# Revit family: Cabinet_Wall_Doors
name_source: partatom
category: Casework
units: mm (PartAtom-declared; Revit-internal decimal feet)

## family parameters
Always vertical = Yes
Classification Number = 23.40.35.11.11
Cut with Voids When Loaded = No
Room Calculation Point = No
Shared = No
Work Plane-Based = No

## types (160) — shared parameters
Assembly Code = C1030410
Building Codes = http://www.iccsafe.org
Construction Details = http://www.arcat.com
Default Elevation = 0' - 0"
Depth = 1' - 0"
Door Finish = <By Category>
Door Frame Material = ARCAT - Wood - Cherry_Domestic
Door Panel Material = ARCAT - Wood - Cherry_Domestic
Door Thickness = 0' - 0 3/4"
Expected Lifespan (Years) = 20
Frame Finish = ARCAT - Wood - Maple_Hard
Frame Width = 0' - 1 1/2"
FrameReveal = 0' - 0 1/4"
Glass Type = ARCAT - Glass - Annealed - Tinted_Green
Green Building-LEED = http://www.arcat.com
Hardware Type = Recessed Cup Self Closing Hinges
Installation Phase = Finish Carpentry
Installation_Fabricaton = http://www.nkba.org
Keynote = 12350
Left Side Panel Finish = ARCAT - Wood - Maple_Hard
Maintainence Schedule (Months) = 1
Manufacturer = Generic
Manufacturer Fax = (203) 939-2444
Manufacturer Website = http://www.arcat.com
Mounting Height = 4' - 6"
Panel Thickness = 0' - 0 3/4"
Product Data = http://www.arcat.com
Product Properties = http://www.arcat.com
Right Side Panel Finish = ARCAT - Wood - Maple_Hard
Specification = http://www.arcat.com
Warranty Duration (Years) = 5

## per-type parameters (varying)
| type | Description | Door Style | DoorCount | Height | Model | Width |
| 42x42h - 2Dr_Glz | 42"W x 42"H 2 Glass Door Wall Cabinet | Door - Shaker-Glass : Door | 2 | 3' - 6" | 42x42h - 2Dr - Glz | 3' - 6" |
| 36x42h - 2Dr_Glz | 36"W x 42"H 2 Glass Door Wall Cabinet | Door - Shaker-Glass : Door | 2 | 3' - 6" | 36x42h - 2Dr - Glz | 3' - 0" |
| 30x42h - 2Dr_Glz | 30"W x 42"H 2 Glass Door Wall Cabinet | Door - Shaker-Glass : Door | 2 | 3' - 6" | 30x42h - 2Dr - Glz | 2' - 6" |
| 24x42h - 2Dr_Glz | 24"W x 42"H 2 Glass Door Wall Cabinet | Door - Shaker-Glass : Door | 2 | 3' - 6" | 24x42h - 2Dr - Glz | 2' - 0" |
| 21x42h - 2Dr_Glz | 21"W x 42"H 2 Glass Door Wall Cabinet | Door - Shaker-Glass : Door | 2 | 3' - 6" | 21x42h - 2Dr - Glz | 1' - 9" |
| 21x42h - 1Dr_Glz | 21"W x 42"H 1 Glass Door Wall Cabinet | Door - Shaker-Glass : Door | 1 | 3' - 6" | 21x42h - 1Dr - Glz | 1' - 9" |
| 18x42h - 2Dr_Glz | 18"W x 42"H 2 Glass Door Wall Cabinet | Door - Shaker-Glass : Door | 2 | 3' - 6" | 18x42h - 2Dr - Glz | 1' - 6" |
| 18x42h - 1Dr_Glz | 18"W x 42"H 1 Glass Door Wall Cabinet | Door - Shaker-Glass : Door | 1 | 3' - 6" | 18x42h - 1Dr - Glz | 1' - 6" |
| 15x42h - 1Dr_Glz | 15"W x 42"H 1 Glass Door Wall Cabinet | Door - Shaker-Glass : Door | 1 | 3' - 6" | 15x42h - 1Dr - Glz | 1' - 3" |
| 12x42h - 1Dr_Glz | 12"W x 42"H 1 Glass Door Wall Cabinet | Door - Shaker-Glass : Door | 1 | 3' - 6" | 12x42h - 1Dr - Glz | 1' - 0" |
| 42x42h - 2Dr | 42"W x 42"H 2 Door Wall Cabinet | Door - Shaker : Door | 2 | 3' - 6" | 42x42h - 2Dr | 3' - 6" |
| 36x42h - 2Dr | 36"W x 42"H 2 Door Wall Cabinet | Door - Shaker : Door | 2 | 3' - 6" | 36x42h - 2Dr | 3' - 0" |
| 30x42h - 2Dr | 30"W x 42"H 2 Door Wall Cabinet | Door - Shaker : Door | 2 | 3' - 6" | 30x42h - 2Dr | 2' - 6" |
| 24x42h - 2Dr | 24"W x 42"H 2 Door Wall Cabinet | Door - Shaker : Door | 2 | 3' - 6" | 24x42h - 2Dr | 2' - 0" |
| 21x42h - 2Dr | 21"W x 42"H 2 Door Wall Cabinet | Door - Shaker : Door | 2 | 3' - 6" | 21x42h - 2Dr | 1' - 9" |
| 21x42h - 1Dr | 21"W x 42"H 1 Door Wall Cabinet | Door - Shaker : Door | 1 | 3' - 6" | 21x42h - 1Dr | 1' - 9" |
| 18x42h - 2Dr | 18"W x 42"H 2 Door Wall Cabinet | Door - Shaker : Door | 2 | 3' - 6" | 18x42h - 2Dr | 1' - 6" |
| 18x42h - 1Dr | 18"W x 42"H 1 Door Wall Cabinet | Door - Shaker : Door | 1 | 3' - 6" | 18x42h - 1Dr | 1' - 6" |
| 15x42h - 1Dr | 15"W x 42"H 1 Door Wall Cabinet | Door - Shaker : Door | 1 | 3' - 6" | 15x42h - 1Dr | 1' - 3" |
| 12x42h - 1Dr | 12"W x 42"H 1 Door Wall Cabinet | Door - Shaker : Door | 1 | 3' - 6" | 12x42h - 1Dr | 1' - 0" |
| 42x36h - 2Dr_Glz | 42"W x 36"H 2 Glass Door Wall Cabinet | Door - Shaker-Glass : Door | 2 | 3' - 0" | 42x36h - 2Dr - Glz | 3' - 6" |
| 36x36h - 2Dr_Glz | 36"W x 36"H 2 Glass Door Wall Cabinet | Door - Shaker-Glass : Door | 2 | 3' - 0" | 36x36h - 2Dr - Glz | 3' - 0" |
| 30x36h - 2Dr_Glz | 30"W x 36"H 2 Glass Door Wall Cabinet | Door - Shaker-Glass : Door | 2 | 3' - 0" | 30x36h - 2Dr - Glz | 2' - 6" |
| 24x36h - 2Dr_Glz | 24"W x 36"H 2 Glass Door Wall Cabinet | Door - Shaker-Glass : Door | 2 | 3' - 0" | 24x36h - 2Dr - Glz | 2' - 0" |
| 21x36h - 2Dr_Glz | 21"W x 36"H 2 Glass Door Wall Cabinet | Door - Shaker-Glass : Door | 2 | 3' - 0" | 21x36h - 2Dr - Glz | 1' - 9" |
| 21x36h - 1Dr_Glz | 21"W x 36"H 1 Glass Door Wall Cabinet | Door - Shaker-Glass : Door | 1 | 3' - 0" | 21x36h - 1Dr - Glz | 1' - 9" |
| 18x36h - 2Dr_Glz | 18"W x 36"H 2 Glass Door Wall Cabinet | Door - Shaker-Glass : Door | 2 | 3' - 0" | 18x36h - 2Dr - Glz | 1' - 6" |
| 18x36h - 1Dr_Glz | 18"W x 36"H 1 Glass Door Wall Cabinet | Door - Shaker-Glass : Door | 1 | 3' - 0" | 18x36h - 1Dr - Glz | 1' - 6" |
| 15x36h - 1Dr_Glz | 15"W x 36"H 1 Glass Door Wall Cabinet | Door - Shaker-Glass : Door | 1 | 3' - 0" | 15x36h - 1Dr - Glz | 1' - 3" |
| 12x36h - 1Dr_Glz | 12"W x 36"H 1 Glass Door Wall Cabinet | Door - Shaker-Glass : Door | 1 | 3' - 0" | 12x36h - 1Dr - Glz | 1' - 0" |
| 42x36h - 2Dr | 42"W x 36"H 2 Door Wall Cabinet | Door - Shaker : Door | 2 | 3' - 0" | 42x36h - 2Dr | 3' - 6" |
| 36x36h - 2Dr | 36"W x 36"H 2 Door Wall Cabinet | Door - Shaker : Door | 2 | 3' - 0" | 36x36h - 2Dr | 3' - 0" |
| 30x36h - 2Dr | 30"W x 36"H 2 Door Wall Cabinet | Door - Shaker : Door | 2 | 3' - 0" | 30x36h - 2Dr | 2' - 6" |
| 24x36h - 2Dr | 24"W x 36"H 2 Door Wall Cabinet | Door - Shaker : Door | 2 | 3' - 0" | 24x36h - 2Dr | 2' - 0" |
| 21x36h - 2Dr | 21"W x 36"H 2 Door Wall Cabinet | Door - Shaker : Door | 2 | 3' - 0" | 21x36h - 2Dr | 1' - 9" |
| 21x36h - 1Dr | 21"W x 36"H 1 Door Wall Cabinet | Door - Shaker : Door | 1 | 3' - 0" | 21x36h - 1Dr | 1' - 9" |
| 18x36h - 2Dr | 18"W x 36"H 2 Door Wall Cabinet | Door - Shaker : Door | 2 | 3' - 0" | 18x36h - 2Dr | 1' - 6" |
| 18x36h - 1Dr | 18"W x 36"H 1 Door Wall Cabinet | Door - Shaker : Door | 1 | 3' - 0" | 18x36h - 1Dr | 1' - 6" |
| 15x36h - 1Dr | 15"W x 36"H 1 Door Wall Cabinet | Door - Shaker : Door | 1 | 3' - 0" | 15x36h - 1Dr | 1' - 3" |
| 12x36h - 1Dr | 12"W x 36"H 1 Door Wall Cabinet | Door - Shaker : Door | 1 | 3' - 0" | 12x36h - 1Dr | 1' - 0" |
| 42x30h - 2Dr_Glz | 42"W x 30"H 2 Glass Door Wall Cabinet | Door - Shaker-Glass : Door | 2 | 2' - 6" | 42x30h - 2Dr - Glz | 3' - 6" |
| 36x30h - 2Dr_Glz | 36"W x 30"H 2 Glass Door Wall Cabinet | Door - Shaker-Glass : Door | 2 | 2' - 6" | 36x30h - 2Dr - Glz | 3' - 0" |
| 30x30h - 2Dr_Glz | 30"W x 30"H 2 Glass Door Wall Cabinet | Door - Shaker-Glass : Door | 2 | 2' - 6" | 30x30h - 2Dr - Glz | 2' - 6" |
| 24x30h - 2Dr_Glz | 24"W x 30"H 2 Glass Door Wall Cabinet | Door - Shaker-Glass : Door | 2 | 2' - 6" | 24x30h - 2Dr - Glz | 2' - 0" |
| 21x30h - 2Dr_Glz | 21"W x 30"H 2 Glass Door Wall Cabinet | Door - Shaker-Glass : Door | 2 | 2' - 6" | 21x30h - 2Dr - Glz | 1' - 9" |
| 21x30h - 1Dr_Glz | 21"W x 30"H 1 Glass Door Wall Cabinet | Door - Shaker-Glass : Door | 1 | 2' - 6" | 21x30h - 1Dr - Glz | 1' - 9" |
| 18x30h - 2Dr_Glz | 18"W x 30"H 2 Glass Door Wall Cabinet | Door - Shaker-Glass : Door | 2 | 2' - 6" | 18x30h - 2Dr - Glz | 1' - 6" |
| 18x30h - 1Dr_Glz | 18"W x 30"H 1 Glass Door Wall Cabinet | Door - Shaker-Glass : Door | 1 | 2' - 6" | 18x30h - 1Dr - Glz | 1' - 6" |
| 15x30h - 1Dr_Glz | 15"W x 30"H 1 Glass Door Wall Cabinet | Door - Shaker-Glass : Door | 1 | 2' - 6" | 15x30h - 1Dr - Glz | 1' - 3" |
| 12x30h - 1Dr_Glz | 12"W x 30"H 1 Glass Door Wall Cabinet | Door - Shaker-Glass : Door | 1 | 2' - 6" | 12x30h - 1Dr - Glz | 1' - 0" |
| 42x30h - 2Dr | 42"W x 30"H 2 Door Wall Cabinet | Door - Shaker : Door | 2 | 2' - 6" | 42x30h - 2Dr | 3' - 6" |
| 36x30h - 2Dr | 36"W x 30"H 2 Door Wall Cabinet | Door - Shaker : Door | 2 | 2' - 6" | 36x30h - 2Dr | 3' - 0" |
| 30x30h - 2Dr | 30"W x 30"H 2 Door Wall Cabinet | Door - Shaker : Door | 2 | 2' - 6" | 30x30h - 2Dr | 2' - 6" |
| 24x30h - 2Dr | 24"W x 30"H 2 Door Wall Cabinet | Door - Shaker : Door | 2 | 2' - 6" | 24x30h - 2Dr | 2' - 0" |
| 21x30h - 2Dr | 21"W x 30"H 2 Door Wall Cabinet | Door - Shaker : Door | 2 | 2' - 6" | 21x30h - 2Dr | 1' - 9" |
| 21x30h - 1Dr | 21"W x 30"H 1 Door Wall Cabinet | Door - Shaker : Door | 1 | 2' - 6" | 21x30h - 1Dr | 1' - 9" |
| 18x30h - 2Dr | 18"W x 30"H 2 Door Wall Cabinet | Door - Shaker : Door | 2 | 2' - 6" | 18x30h - 2Dr | 1' - 6" |
| 18x30h - 1Dr | 18"W x 30"H 1 Door Wall Cabinet | Door - Shaker : Door | 1 | 2' - 6" | 18x30h - 1Dr | 1' - 6" |
| 15x30h - 1Dr | 15"W x 30"H 1 Door Wall Cabinet | Door - Shaker : Door | 1 | 2' - 6" | 15x30h - 1Dr | 1' - 3" |
| 12x30h - 1Dr | 12"W x 30"H 1 Door Wall Cabinet | Door - Shaker : Door | 1 | 2' - 6" | 12x30h - 1Dr | 1' - 0" |
| 42x21h - 2Dr_Glz | 42"W x 21"H 2 Glass Door Wall Cabinet | Door - Shaker-Glass : Door | 2 | 1' - 9" | 42x21h - 2Dr - Glz | 3' - 6" |
| 36x21h - 2Dr_Glz | 36"W x 21"H 2 Glass Door Wall Cabinet | Door - Shaker-Glass : Door | 2 | 1' - 9" | 36x21h - 2Dr - Glz | 3' - 0" |
| 30x21h - 2Dr_Glz | 30"W x 21"H 2 Glass Door Wall Cabinet | Door - Shaker-Glass : Door | 2 | 1' - 9" | 30x21h - 2Dr - Glz | 2' - 6" |
| 24x21h - 2Dr_Glz | 24"W x 21"H 2 Glass Door Wall Cabinet | Door - Shaker-Glass : Door | 2 | 1' - 9" | 24x21h - 2Dr - Glz | 2' - 0" |
| 21x21h - 2Dr_Glz | 21"W x 21"H 2 Glass Door Wall Cabinet | Door - Shaker-Glass : Door | 2 | 1' - 9" | 21x21h - 2Dr - Glz | 1' - 9" |
| 21x21h - 1Dr_Glz | 21"W x 21"H 1 Glass Door Wall Cabinet | Door - Shaker-Glass : Door | 1 | 1' - 9" | 21x21h - 1Dr - Glz | 1' - 9" |
| 18x21h - 2Dr_Glz | 18"W x 21"H 2 Glass Door Wall Cabinet | Door - Shaker-Glass : Door | 2 | 1' - 9" | 18x21h - 2Dr - Glz | 1' - 6" |
| 18x21h - 1Dr_Glz | 18"W x 21"H 1 Glass Door Wall Cabinet | Door - Shaker-Glass : Door | 1 | 1' - 9" | 18x21h - 1Dr - Glz | 1' - 6" |
| 15x21h - 1Dr_Glz | 15"W x 21"H 1 Glass Door Wall Cabinet | Door - Shaker-Glass : Door | 1 | 1' - 9" | 15x21h - 1Dr - Glz | 1' - 3" |
| 12x21h - 1Dr_Glz | 12"W x 21"H 1 Glass Door Wall Cabinet | Door - Shaker-Glass : Door | 1 | 1' - 9" | 12x21h - 1Dr - Glz | 1' - 0" |
| 42x21h - 2Dr | 42"W x 21"H 2 Door Wall Cabinet | Door - Shaker : Door | 2 | 1' - 9" | 42x21h - 2Dr | 3' - 6" |
| 36x21h - 2Dr | 36"W x 21"H 2 Door Wall Cabinet | Door - Shaker : Door | 2 | 1' - 9" | 36x21h - 2Dr | 3' - 0" |
| 30x21h - 2Dr | 30"W x 21"H 2 Door Wall Cabinet | Door - Shaker : Door | 2 | 1' - 9" | 30x21h - 2Dr | 2' - 6" |
| 24x21h - 2Dr | 24"W x 21"H 2 Door Wall Cabinet | Door - Shaker : Door | 2 | 1' - 9" | 24x21h - 2Dr | 2' - 0" |
| 21x21h - 2Dr | 21"W x 21"H 2 Door Wall Cabinet | Door - Shaker : Door | 2 | 1' - 9" | 21x21h - 2Dr | 1' - 9" |
| 21x21h - 1Dr | 21"W x 21"H 1 Door Wall Cabinet | Door - Shaker : Door | 1 | 1' - 9" | 21x21h - 1Dr | 1' - 9" |
| 18x21h - 2Dr | 18"W x 21"H 2 Door Wall Cabinet | Door - Shaker : Door | 2 | 1' - 9" | 18x21h - 2Dr | 1' - 6" |
| 18x21h - 1Dr | 18"W x 21"H 1 Door Wall Cabinet | Door - Shaker : Door | 1 | 1' - 9" | 18x21h - 1Dr | 1' - 6" |
| 15x21h - 1Dr | 15"W x 21"H 1 Door Wall Cabinet | Door - Shaker : Door | 1 | 1' - 9" | 15x21h - 1Dr | 1' - 3" |
| 12x21h - 1Dr | 12"W x 21"H 1 Door Wall Cabinet | Door - Shaker : Door | 1 | 1' - 9" | 12x21h - 1Dr | 1' - 0" |
| 42x18h - 2Dr_Glz | 42"W x 18"H 2 Glass Door Wall Cabinet | Door - Shaker-Glass : Door | 2 | 1' - 6" | 42x18h - 2Dr - Glz | 3' - 6" |
| 36x18h - 2Dr_Glz | 36"W x 18"H 2 Glass Door Wall Cabinet | Door - Shaker-Glass : Door | 2 | 1' - 6" | 36x18h - 2Dr - Glz | 3' - 0" |
| 30x18h - 2Dr_Glz | 30"W x 18"H 2 Glass Door Wall Cabinet | Door - Shaker-Glass : Door | 2 | 1' - 6" | 30x18h - 2Dr - Glz | 2' - 6" |
| 24x18h - 2Dr_Glz | 24"W x 18"H 2 Glass Door Wall Cabinet | Door - Shaker-Glass : Door | 2 | 1' - 6" | 24x18h - 2Dr - Glz | 2' - 0" |
| 21x18h - 2Dr_Glz | 21"W x 18"H 2 Glass Door Wall Cabinet | Door - Shaker-Glass : Door | 2 | 1' - 6" | 21x18h - 2Dr - Glz | 1' - 9" |
| 21x18h - 1Dr_Glz | 21"W x 18"H 1 Glass Door Wall Cabinet | Door - Shaker-Glass : Door | 1 | 1' - 6" | 21x18h - 1Dr - Glz | 1' - 9" |
| 18x18h - 2Dr_Glz | 18"W x 18"H 2 Glass Door Wall Cabinet | Door - Shaker-Glass : Door | 2 | 1' - 6" | 18x18h - 2Dr - Glz | 1' - 6" |
| 18x18h - 1Dr_Glz | 18"W x 18"H 1 Glass Door Wall Cabinet | Door - Shaker-Glass : Door | 1 | 1' - 6" | 18x18h - 1Dr - Glz | 1' - 6" |
| 15x18h - 1Dr_Glz | 15"W x 18"H 1 Glass Door Wall Cabinet | Door - Shaker-Glass : Door | 1 | 1' - 6" | 15x18h - 1Dr - Glz | 1' - 3" |
| 12x18h - 1Dr_Glz | 12"W x 18"H 1 Glass Door Wall Cabinet | Door - Shaker-Glass : Door | 1 | 1' - 6" | 12x18h - 1Dr - Glz | 1' - 0" |
| 42x18h - 2Dr | 42"W x 18"H 2 Door Wall Cabinet | Door - Shaker : Door | 2 | 1' - 6" | 42x18h - 2Dr | 3' - 6" |
| 36x18h - 2Dr | 36"W x 18"H 2 Door Wall Cabinet | Door - Shaker : Door | 2 | 1' - 6" | 36x18h - 2Dr | 3' - 0" |
| 30x18h - 2Dr | 30"W x 18"H 2 Door Wall Cabinet | Door - Shaker : Door | 2 | 1' - 6" | 30x18h - 2Dr | 2' - 6" |
| 24x18h - 2Dr | 24"W x 18"H 2 Door Wall Cabinet | Door - Shaker : Door | 2 | 1' - 6" | 24x18h - 2Dr | 2' - 0" |
| 21x18h - 2Dr | 21"W x 18"H 2 Door Wall Cabinet | Door - Shaker : Door | 2 | 1' - 6" | 21x18h - 2Dr | 1' - 9" |
| 21x18h - 1Dr | 21"W x 18"H 1 Door Wall Cabinet | Door - Shaker : Door | 1 | 1' - 6" | 21x18h - 1Dr | 1' - 9" |
| 18x18h - 2Dr | 18"W x 18"H 2 Door Wall Cabinet | Door - Shaker : Door | 2 | 1' - 6" | 18x18h - 2Dr | 1' - 6" |
| 18x18h - 1Dr | 18"W x 18"H 1 Door Wall Cabinet | Door - Shaker : Door | 1 | 1' - 6" | 18x18h - 1Dr | 1' - 6" |
| 15x18h - 1Dr | 15"W x 18"H 1 Door Wall Cabinet | Door - Shaker : Door | 1 | 1' - 6" | 15x18h - 1Dr | 1' - 3" |
| 12x18h - 1Dr | 12"W x 18"H 1 Door Wall Cabinet | Door - Shaker : Door | 1 | 1' - 6" | 12x18h - 1Dr | 1' - 0" |
| 42x15h - 2Dr_Glz | 42"W x 15"H 2 Glass Door Wall Cabinet | Door - Shaker-Glass : Door | 2 | 1' - 3" | 42x15h - 2Dr - Glz | 3' - 6" |
| 36x15h - 2Dr_Glz | 36"W x 15"H 2 Glass Door Wall Cabinet | Door - Shaker-Glass : Door | 2 | 1' - 3" | 36x15h - 2Dr - Glz | 3' - 0" |
| 30x15h - 2Dr_Glz | 30"W x 15"H 2 Glass Door Wall Cabinet | Door - Shaker-Glass : Door | 2 | 1' - 3" | 30x15h - 2Dr - Glz | 2' - 6" |
| 24x15h - 2Dr_Glz | 24"W x 15"H 2 Glass Door Wall Cabinet | Door - Shaker-Glass : Door | 2 | 1' - 3" | 24x15h - 2Dr - Glz | 2' - 0" |
| 21x15h - 2Dr_Glz | 21"W x 15"H 2 Glass Door Wall Cabinet | Door - Shaker-Glass : Door | 2 | 1' - 3" | 21x15h - 2Dr - Glz | 1' - 9" |
| 21x15h - 1Dr_Glz | 21"W x 15"H 1 Glass Door Wall Cabinet | Door - Shaker-Glass : Door | 1 | 1' - 3" | 21x15h - 1Dr - Glz | 1' - 9" |
| 18x15h - 2Dr_Glz | 18"W x 15"H 2 Glass Door Wall Cabinet | Door - Shaker-Glass : Door | 2 | 1' - 3" | 18x15h - 2Dr - Glz | 1' - 6" |
| 18x15h - 1Dr_Glz | 18"W x 15"H 1 Glass Door Wall Cabinet | Door - Shaker-Glass : Door | 1 | 1' - 3" | 18x15h - 1Dr - Glz | 1' - 6" |
| 15x15h - 1Dr_Glz | 15"W x 15"H 1 Glass Door Wall Cabinet | Door - Shaker-Glass : Door | 1 | 1' - 3" | 15x15h - 1Dr - Glz | 1' - 3" |
| 12x15h - 1Dr_Glz | 12"W x 15"H 1 Glass Door Wall Cabinet | Door - Shaker-Glass : Door | 1 | 1' - 3" | 12x15h - 1Dr - Glz | 1' - 0" |
| 42x15h - 2Dr | 42"W x 15"H 2 Door Wall Cabinet | Door - Shaker : Door | 2 | 1' - 3" | 42x15h - 2Dr | 3' - 6" |
| 36x15h - 2Dr | 36"W x 15"H 2 Door Wall Cabinet | Door - Shaker : Door | 2 | 1' - 3" | 36x15h - 2Dr | 3' - 0" |
| 30x15h - 2Dr | 30"W x 15"H 2 Door Wall Cabinet | Door - Shaker : Door | 2 | 1' - 3" | 30x15h - 2Dr | 2' - 6" |
| 24x15h - 2Dr | 24"W x 15"H 2 Door Wall Cabinet | Door - Shaker : Door | 2 | 1' - 3" | 24x15h - 2Dr | 2' - 0" |
| 21x15h - 2Dr | 21"W x 15"H 2 Door Wall Cabinet | Door - Shaker : Door | 2 | 1' - 3" | 21x15h - 2Dr | 1' - 9" |
| 21x15h - 1Dr | 21"W x 15"H 1 Door Wall Cabinet | Door - Shaker : Door | 1 | 1' - 3" | 21x15h - 1Dr | 1' - 9" |
| 18x15h - 2Dr | 18"W x 15"H 2 Door Wall Cabinet | Door - Shaker : Door | 2 | 1' - 3" | 18x15h - 2Dr | 1' - 6" |
| 18x15h - 1Dr | 18"W x 15"H 1 Door Wall Cabinet | Door - Shaker : Door | 1 | 1' - 3" | 18x15h - 1Dr | 1' - 6" |
| 15x15h - 1Dr | 15"W x 15"H 1 Door Wall Cabinet | Door - Shaker : Door | 1 | 1' - 3" | 15x15h - 1Dr | 1' - 3" |
| 12x15h - 1Dr | 12"W x 15"H 1 Door Wall Cabinet | Door - Shaker : Door | 1 | 1' - 3" | 12x15h - 1Dr | 1' - 0" |
| 42x12h - 2Dr_Glz | 42"W x 12"H 2 Glass Door Wall Cabinet | Door - Shaker-Glass : Door | 2 | 1' - 0" | 42x12h - 2Dr - Glz | 3' - 6" |
| 36x12h - 2Dr_Glz | 36"W x 12"H 2 Glass Door Wall Cabinet | Door - Shaker-Glass : Door | 2 | 1' - 0" | 36x12h - 2Dr - Glz | 3' - 0" |
| 30x12h - 2Dr_Glz | 30"W x 12"H 2 Glass Door Wall Cabinet | Door - Shaker-Glass : Door | 2 | 1' - 0" | 30x12h - 2Dr - Glz | 2' - 6" |
| 24x12h - 2Dr_Glz | 24"W x 12"H 2 Glass Door Wall Cabinet | Door - Shaker-Glass : Door | 2 | 1' - 0" | 24x12h - 2Dr - Glz | 2' - 0" |
| 21x12h - 2Dr_Glz | 21"W x 12"H 2 Glass Door Wall Cabinet | Door - Shaker-Glass : Door | 2 | 1' - 0" | 21x12h - 2Dr - Glz | 1' - 9" |
| 21x12h - 1Dr_Glz | 21"W x 12"H 1 Glass Door Wall Cabinet | Door - Shaker-Glass : Door | 1 | 1' - 0" | 21x12h - 1Dr - Glz | 1' - 9" |
| 18x12h - 2Dr_Glz | 18"W x 12"H 2 Glass Door Wall Cabinet | Door - Shaker-Glass : Door | 2 | 1' - 0" | 18x12h - 2Dr - Glz | 1' - 6" |
| 18x12h - 1Dr_Glz | 18"W x 12"H 1 Glass Door Wall Cabinet | Door - Shaker-Glass : Door | 1 | 1' - 0" | 18x12h - 1Dr - Glz | 1' - 6" |
| 15x12h - 1Dr_Glz | 15"W x 12"H 1 Glass Door Wall Cabinet | Door - Shaker-Glass : Door | 1 | 1' - 0" | 15x12h - 1Dr - Glz | 1' - 3" |
| 12x12h - 1Dr_Glz | 12"W x 12"H 1 Glass Door Wall Cabinet | Door - Shaker-Glass : Door | 1 | 1' - 0" | 12x12h - 1Dr - Glz | 1' - 0" |
| 42x12h - 2Dr | 42"W x 12"H 2 Door Wall Cabinet | Door - Shaker : Door | 2 | 1' - 0" | 42x12h - 2Dr | 3' - 6" |
| 36x12h - 2Dr | 36"W x 12"H 2 Door Wall Cabinet | Door - Shaker : Door | 2 | 1' - 0" | 36x12h - 2Dr | 3' - 0" |
| 30x12h - 2Dr | 30"W x 12"H 2 Door Wall Cabinet | Door - Shaker : Door | 2 | 1' - 0" | 30x12h - 2Dr | 2' - 6" |
| 24x12h - 2Dr | 24"W x 12"H 2 Door Wall Cabinet | Door - Shaker : Door | 2 | 1' - 0" | 24x12h - 2Dr | 2' - 0" |
| 21x12h - 2Dr | 21"W x 12"H 2 Door Wall Cabinet | Door - Shaker : Door | 2 | 1' - 0" | 21x12h - 2Dr | 1' - 9" |
| 21x12h - 1Dr | 21"W x 12"H 1 Door Wall Cabinet | Door - Shaker : Door | 1 | 1' - 0" | 21x12h - 1Dr | 1' - 9" |
| 18x12h - 2Dr | 18"W x 12"H 2 Door Wall Cabinet | Door - Shaker : Door | 2 | 1' - 0" | 18x12h - 2Dr | 1' - 6" |
| 18x12h - 1Dr | 18"W x 12"H 1 Door Wall Cabinet | Door - Shaker : Door | 1 | 1' - 0" | 18x12h - 1Dr | 1' - 6" |
| 15x12h - 1Dr | 15"W x 12"H 1 Door Wall Cabinet | Door - Shaker : Door | 1 | 1' - 0" | 15x12h - 1Dr | 1' - 3" |
| 12x12h - 1Dr | 12"W x 12"H 1 Door Wall Cabinet | Door - Shaker : Door | 1 | 1' - 0" | 12x12h - 1Dr | 1' - 0" |
| 42x24h - 2Dr_Glz | 42"W x 24"H 2 Glass Door Wall Cabinet | Door - Shaker-Glass : Door | 2 | 2' - 0" | 42x24h - 2Dr - Glz | 3' - 6" |
| 36x24h - 2Dr_Glz | 36"W x 24"H 2 Glass Door Wall Cabinet | Door - Shaker-Glass : Door | 2 | 2' - 0" | 36x24h - 2Dr - Glz | 3' - 0" |
| 30x24h - 2Dr_Glz | 30"W x 24"H 2 Glass Door Wall Cabinet | Door - Shaker-Glass : Door | 2 | 2' - 0" | 30x24h - 2Dr - Glz | 2' - 6" |
| 24x24h - 2Dr_Glz | 24"W x 24"H 2 Glass Door Wall Cabinet | Door - Shaker-Glass : Door | 2 | 2' - 0" | 24x24h - 2Dr - Glz | 2' - 0" |
| 21x24h - 2Dr_Glz | 21"W x 24"H 2 Glass Door Wall Cabinet | Door - Shaker-Glass : Door | 2 | 2' - 0" | 21x24h - 2Dr - Glz | 1' - 9" |
| 21x24h - 1Dr_Glz | 21"W x 24"H 1 Glass Door Wall Cabinet | Door - Shaker-Glass : Door | 1 | 2' - 0" | 21x24h - 1Dr - Glz | 1' - 9" |
| 18x24h - 2Dr_Glz | 18"W x 24"H 2 Glass Door Wall Cabinet | Door - Shaker-Glass : Door | 2 | 2' - 0" | 18x24h - 2Dr - Glz | 1' - 6" |
| 18x24h - 1Dr_Glz | 18"W x 24"H 1 Glass Door Wall Cabinet | Door - Shaker-Glass : Door | 1 | 2' - 0" | 18x24h - 1Dr - Glz | 1' - 6" |
| 15x24h - 1Dr_Glz | 15"W x 24"H 1 Glass Door Wall Cabinet | Door - Shaker-Glass : Door | 1 | 2' - 0" | 15x24h - 1Dr - Glz | 1' - 3" |
| 12x24h - 1Dr_Glz | 12"W x 24"H 1 Glass Door Wall Cabinet | Door - Shaker-Glass : Door | 1 | 2' - 0" | 12x24h - 1Dr - Glz | 1' - 0" |
| 42x24h - 2Dr | 42"W x 24"H 2 Door Wall Cabinet | Door - Shaker : Door | 2 | 2' - 0" | 42x24h - 2Dr | 3' - 6" |
| 36x24h - 2Dr | 36"W x 24"H 2 Door Wall Cabinet | Door - Shaker : Door | 2 | 2' - 0" | 36x24h - 2Dr | 3' - 0" |
| 30x24h - 2Dr | 30"W x 24"H 2 Door Wall Cabinet | Door - Shaker : Door | 2 | 2' - 0" | 30x24h - 2Dr | 2' - 6" |
| 24x24h - 2Dr | 24"W x 24"H 2 Door Wall Cabinet | Door - Shaker : Door | 2 | 2' - 0" | 24x24h - 2Dr | 2' - 0" |
| 21x24h - 2Dr | 21"W x 24"H 2 Door Wall Cabinet | Door - Shaker : Door | 2 | 2' - 0" | 21x24h - 2Dr | 1' - 9" |
| 21x24h - 1Dr | 21"W x 24"H 1 Door Wall Cabinet | Door - Shaker : Door | 1 | 2' - 0" | 21x24h - 1Dr | 1' - 9" |
| 18x24h - 2Dr | 18"W x 24"H 2 Door Wall Cabinet | Door - Shaker : Door | 2 | 2' - 0" | 18x24h - 2Dr | 1' - 6" |
| 18x24h - 1Dr | 18"W x 24"H 1 Door Wall Cabinet | Door - Shaker : Door | 1 | 2' - 0" | 18x24h - 1Dr | 1' - 6" |
| 15x24h - 1Dr | 15"W x 24"H 1 Door Wall Cabinet | Door - Shaker : Door | 1 | 2' - 0" | 15x24h - 1Dr | 1' - 3" |
| 12x24h - 1Dr | 12"W x 24"H 1 Door Wall Cabinet | Door - Shaker : Door | 1 | 2' - 0" | 12x24h - 1Dr | 1' - 0" |

## geometry (parser evidence)
native form markers: Blend x2, Sweep x10
no freeform markers — native parametric forms only
